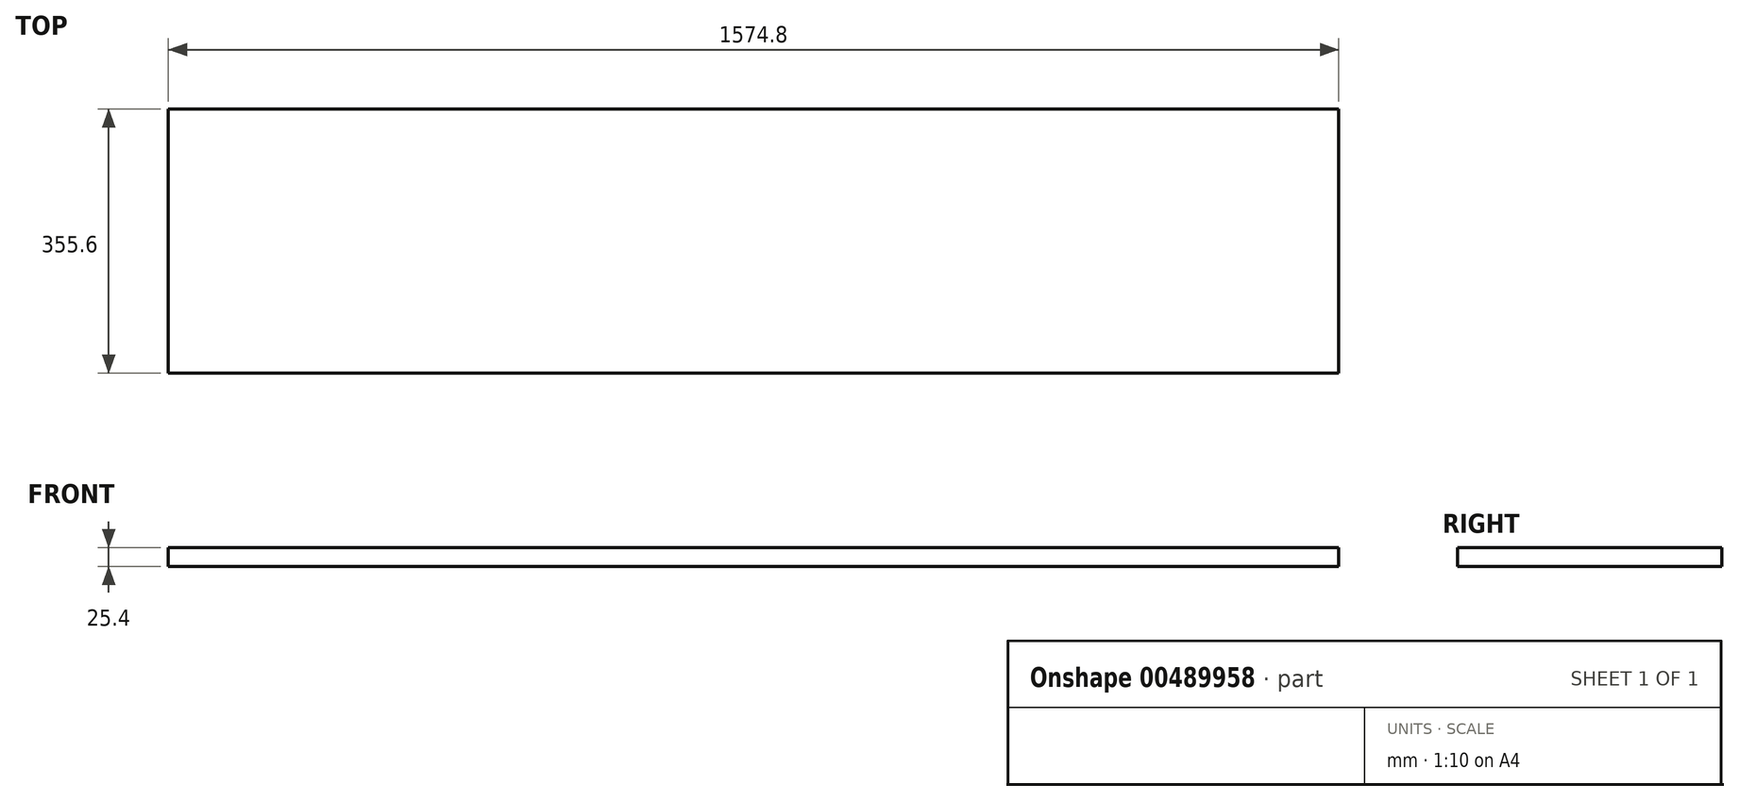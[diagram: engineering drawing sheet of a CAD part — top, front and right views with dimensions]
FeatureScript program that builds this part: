
annotation { "Feature Type Name" : "Feature", "Feature Type Description" : "" }
export const myFeature = defineFeature(function(context is Context, id is Id, definition is map)
    precondition{}
    {
        {
            var Q0;
            Q0=qCreatedBy(makeId("Top.planeOp"),FACE);
            var sketch = newSketch(context, id + "F0", { "sketchPlane" : qUnion([Q0])});
            skLineSegment(sketch, "E0.bottom", {"start": v(-787.4, -177.8) * mm, "end": v(787.4, -177.8) * mm});
            skLineSegment(sketch, "E0.top", {"start": v(-787.4, 177.8) * mm, "end": v(787.4, 177.8) * mm});
            skLineSegment(sketch, "E0.left", {"start": v(-787.4, -177.8) * mm, "end": v(-787.4, 177.8) * mm});
            skLineSegment(sketch, "E0.right", {"start": v(787.4, -177.8) * mm, "end": v(787.4, 177.8) * mm});
            skPoint(sketch, "E0.middle", {"position": v(0, 0) * mm});
            skSolve(sketch);
        }
        {
            var Q0;
            Q0=makeQuery(id+"F0.imprint","IMPRINT",FACE,{"disambiguationData":[TD([[makeQuery(id+"F0.imprint","IMPRINT",EDGE,{"derivedFrom":sQuery(id+"F0.wireOp",EDGE,"E0.bottom")}),1.0]])]});
            extrude(context, id + "F1", {"entities" : qUnion([Q0]), "depth" : 25.4 * mm});
        }
    });
